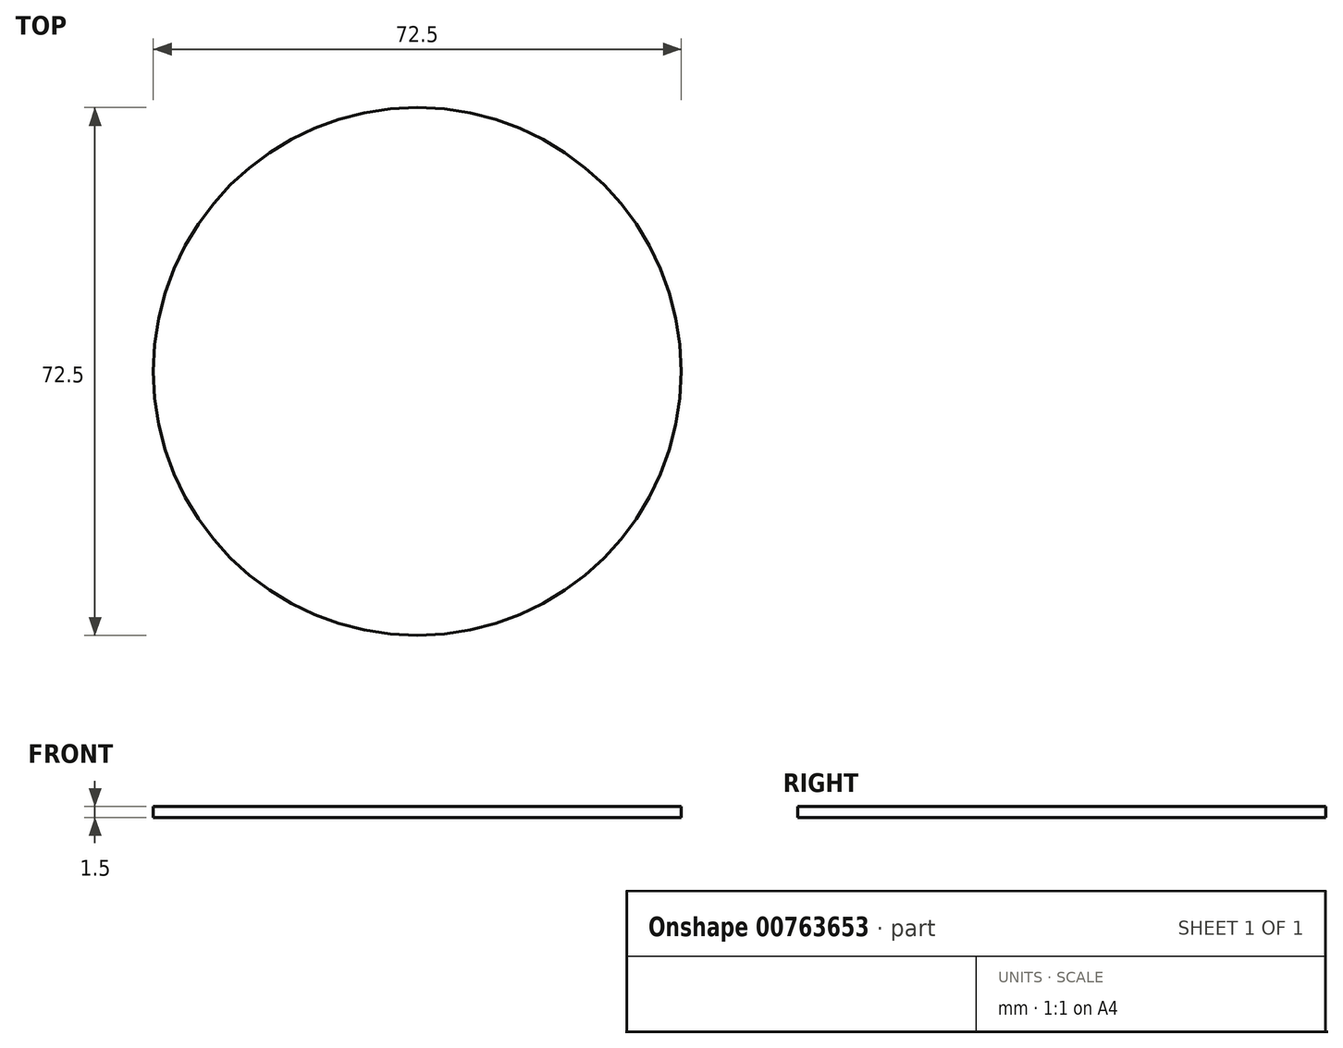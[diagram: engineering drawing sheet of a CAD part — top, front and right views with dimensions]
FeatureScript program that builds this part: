
annotation { "Feature Type Name" : "Feature", "Feature Type Description" : "" }
export const myFeature = defineFeature(function(context is Context, id is Id, definition is map)
    precondition{}
    {
        {
            var Q0;
            Q0=qCreatedBy(makeId("Top.planeOp"),FACE);
            var sketch = newSketch(context, id + "F0", { "sketchPlane" : qUnion([Q0])});
            skCircle(sketch, "E0", {"center": v(0, 0) * mm, "radius": 36.25 * mm});
            skSolve(sketch);
        }
        {
            var Q0;
            Q0 = qSketchRegion(id + "F0", true);
            extrude(context, id + "F1", {"entities" : qUnion([Q0]), "depth" : 1.5 * mm, "offsetDistance" : 25 * mm});
        }
    });
